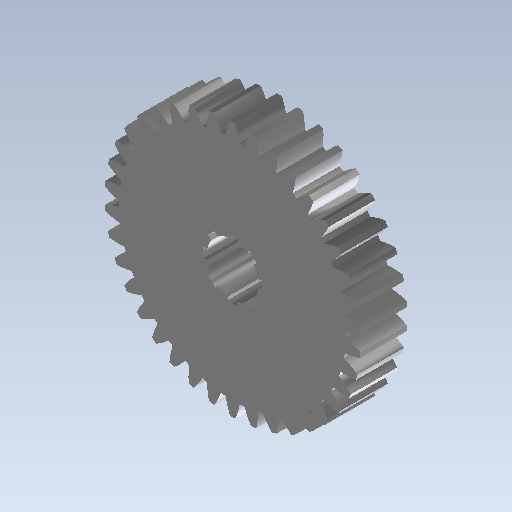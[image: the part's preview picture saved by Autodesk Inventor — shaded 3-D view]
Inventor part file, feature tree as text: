
AUTODESK INVENTOR PART (.ipt)
format: ipt  version: 2020 (Build 240168000, 168)  size: 359,424 bytes
history: native  units: mm (DEFAULTED — no unit token found)
features: sketch x4, extrude x3, plane x3, other x3, pattern_circular x1
ambient origin geometry x8: Origin, YZ Plane, XZ Plane, XY Plane, X Axis, Y Axis, Z Axis, Center Point
bodies: Solid1 (feature_tree)
feature tree (14):
  extrude  "Extrusion1"  Depth=1.8mm TaperAngle=0.0deg
  plane  "Work Plane2"
  plane  "Work Plane8"
  plane  "Work Plane9"
  other  "Цилиндрическое зубчатое зацепление"
  extrude  "Выдавливание2"  Depth=10.0mm TaperAngle=0.0deg
  extrude  "Выдавливание3"  Depth=1.8mm
  pattern_circular  "Круговой массив1"  [2 undecoded]
  sketch  "Sketch1"  dims[d0=9.865mm d1=1.8mm d2=0.0mm]
  sketch  "Sketch2"  dims[d3=9.5mm d4=10.0mm d5=0.0mm d16=6.0mm d17=0.0mm d34=0.826735mm d39=0.0mm d41=0.0mm d43=6.0mm d46=6.0mm d47=0.0mm d48=0.0mm d49=2.0mm d50=10.0mm d51=0.0mm d53=2.3mm d54=3.490659mm d55=1.8mm d56=0.0mm d57=80.0mm d58=360.0deg]
  other  "Srf1"
  sketch  "Эскиз3"
  sketch  "Эскиз4"
  other  "Средний диаметр"
note: 2 required parameter values undecoded (feature->parameter linkage not recoverable at this tier; creation-order binding heuristic only, values carry confidence <= 0.55)
